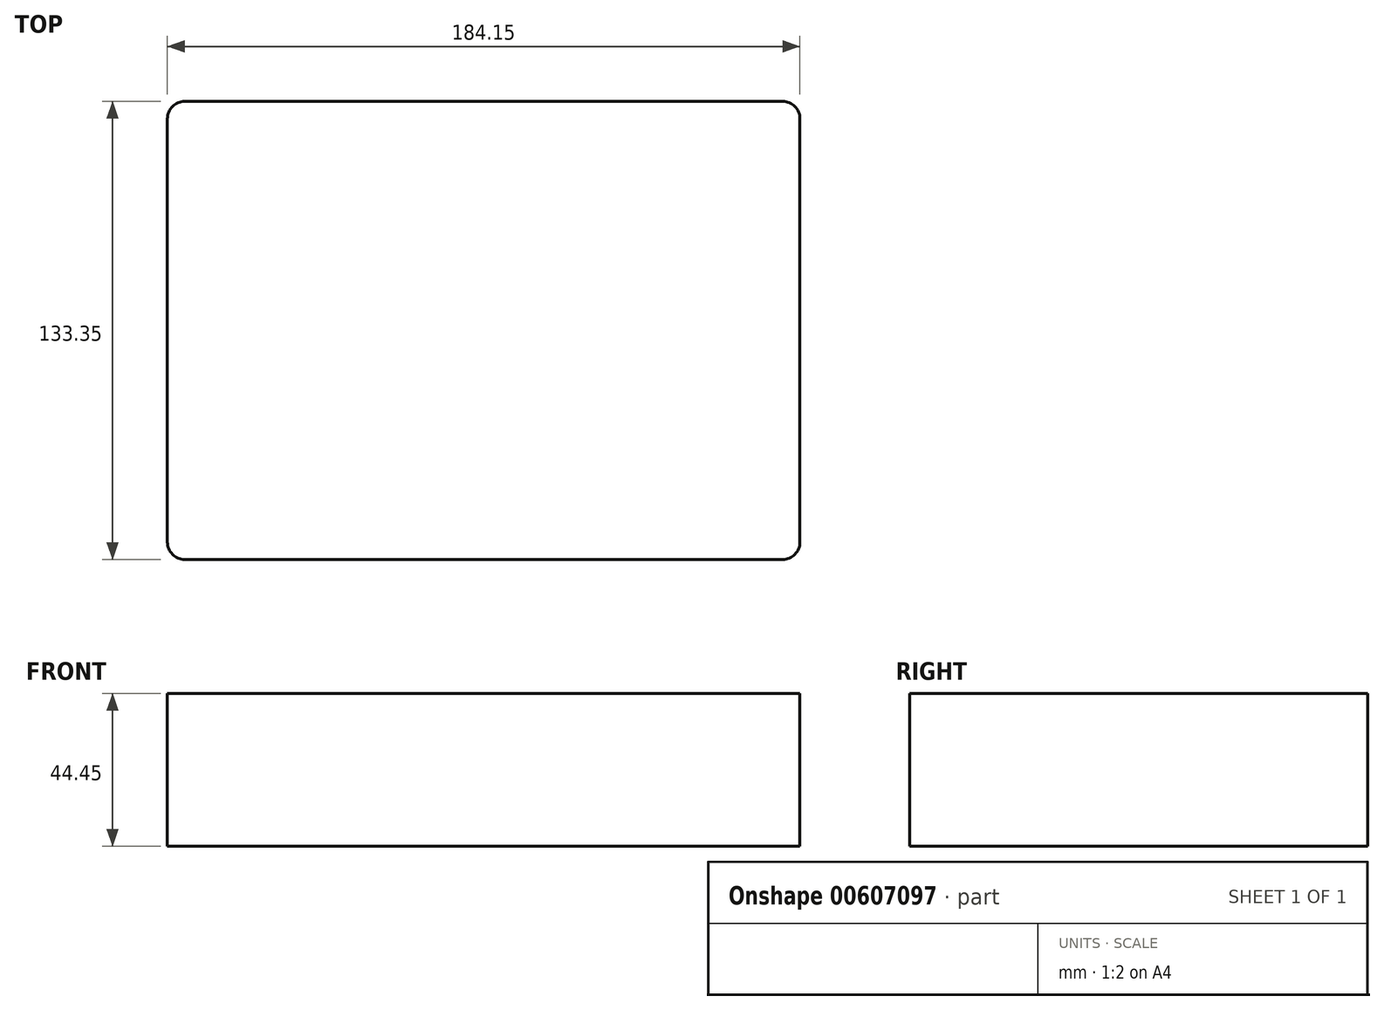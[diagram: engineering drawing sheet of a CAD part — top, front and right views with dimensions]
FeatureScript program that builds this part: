
annotation { "Feature Type Name" : "Feature", "Feature Type Description" : "" }
export const myFeature = defineFeature(function(context is Context, id is Id, definition is map)
    precondition{}
    {
        {
            var Q0;
            Q0=qCreatedBy(makeId("Top.planeOp"),FACE);
            var sketch = newSketch(context, id + "F0", { "sketchPlane" : qUnion([Q0])});
            skLineSegment(sketch, "E0", {"start": v(-128.48, 46.2) * mm, "end": v(55.67, 46.2) * mm});
            skLineSegment(sketch, "E1", {"start": v(55.67, 46.2) * mm, "end": v(55.67, -87.16) * mm});
            skLineSegment(sketch, "E2", {"start": v(-128.48, 46.2) * mm, "end": v(-128.48, -87.16) * mm});
            skLineSegment(sketch, "E3", {"start": v(-128.48, -87.16) * mm, "end": v(55.67, -87.16) * mm});
            skSolve(sketch);
        }
        {
            var Q0;
            Q0 = qSketchRegion(id + "F0", true);
            extrude(context, id + "F1", {"entities" : qUnion([Q0]), "depth" : 44.45 * mm, "offsetDistance" : 25.4 * mm});
        }
        {
            var Q0;
            Q0=makeQuery(id+"F1.opExtrude","SWEPT_EDGE",EDGE,{"disambiguationData":[OSD([sQuery(id+"F0.wireOp",EDGE,"E1"),sQuery(id+"F0.wireOp",EDGE,"E3")])]});
            var Q1;
            Q1=makeQuery(id+"F1.opExtrude","SWEPT_EDGE",EDGE,{"disambiguationData":[OSD([sQuery(id+"F0.wireOp",EDGE,"E0"),sQuery(id+"F0.wireOp",EDGE,"E1")])]});
            var Q2;
            Q2=makeQuery(id+"F1.opExtrude","SWEPT_EDGE",EDGE,{"disambiguationData":[OSD([sQuery(id+"F0.wireOp",EDGE,"E2"),sQuery(id+"F0.wireOp",EDGE,"E3")])]});
            var Q3;
            Q3=makeQuery(id+"F1.opExtrude","SWEPT_EDGE",EDGE,{"disambiguationData":[OSD([sQuery(id+"F0.wireOp",EDGE,"E0"),sQuery(id+"F0.wireOp",EDGE,"E2")])]});
            fillet(context, id + "F2", {"entities" : qUnion([Q0, Q1, Q2, Q3]), "radius" : 5.08 * mm, "tangentPropagation" : true, "allowEdgeOverflow" : false});
        }
    });
